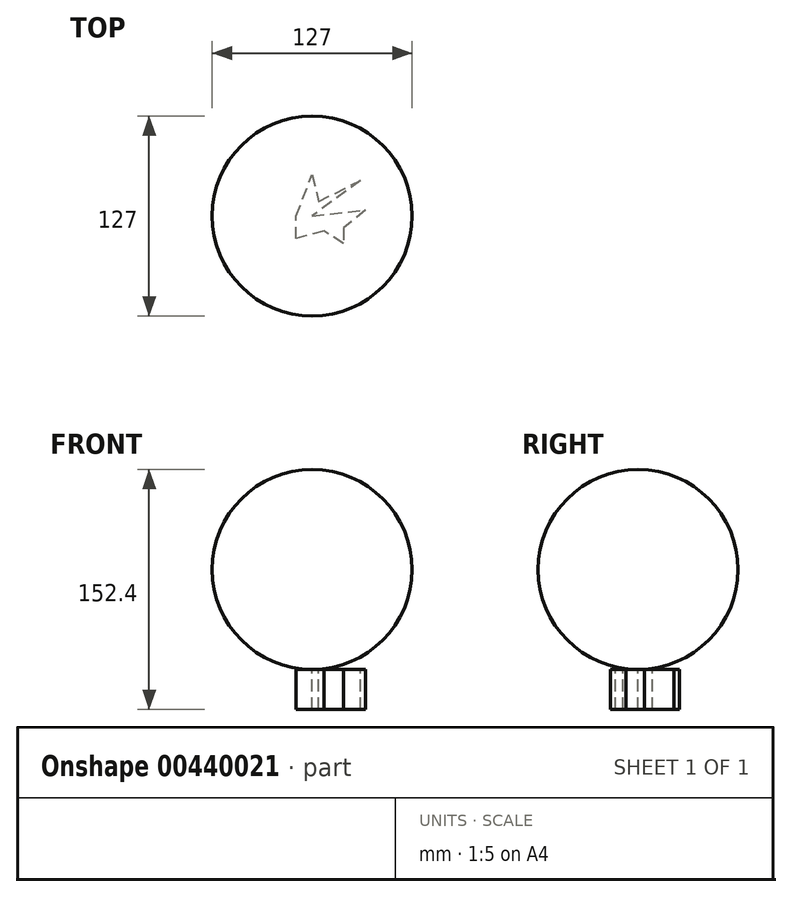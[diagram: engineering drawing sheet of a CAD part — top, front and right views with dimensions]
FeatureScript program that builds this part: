
annotation { "Feature Type Name" : "Feature", "Feature Type Description" : "" }
export const myFeature = defineFeature(function(context is Context, id is Id, definition is map)
    precondition{}
    {
        {
            var Q0;
            Q0=qCreatedBy(makeId("Top.planeOp"),FACE);
            var sketch = newSketch(context, id + "F0", { "sketchPlane" : qUnion([Q0])});
            skCircle(sketch, "E0", {"center": v(0, 0) * mm, "radius": 63.5 * mm});
            skSolve(sketch);
        }
        {
            var Q0;
            Q0=makeQuery(id+"F0.imprint","IMPRINT",FACE,{"disambiguationData":[TD([[makeQuery(id+"F0.imprint","IMPRINT",EDGE,{"derivedFrom":sQuery(id+"F0.wireOp",EDGE,"E0")}),1.0]])]});
            extrude(context, id + "F1", {"entities" : qUnion([Q0]), "depth" : 127 * mm});
        }
        {
            var Q0;
            Q0=makeQuery(id+"F1.opExtrude","CAP_EDGE",EDGE,{"disambiguationData":[OSD([sQuery(id+"F0.wireOp",EDGE,"E0")])],"isStart":false});
            var Q1;
            Q1=makeQuery(id+"F1.opExtrude","CAP_EDGE",EDGE,{"disambiguationData":[OSD([sQuery(id+"F0.wireOp",EDGE,"E0")])],"isStart":true});
            fillet(context, id + "F2", {"entities" : qUnion([Q0, Q1]), "radius" : 63.5 * mm, "tangentPropagation" : true, "allowEdgeOverflow" : false});
        }
        {
            var Q0;
            Q0=qCreatedBy(makeId("Top.planeOp"),FACE);
            var sketch = newSketch(context, id + "F3", { "sketchPlane" : qUnion([Q0])});
            skLineSegment(sketch, "E1", {"start": v(0, 0) * mm, "end": v(33.91, 3.95) * mm});
            skLineSegment(sketch, "E2", {"start": v(33.91, 3.95) * mm, "end": v(19.88, -7.66) * mm});
            skLineSegment(sketch, "E3", {"start": v(19.88, -7.66) * mm, "end": v(19.88, -17.6) * mm});
            skLineSegment(sketch, "E4", {"start": v(19.88, -17.6) * mm, "end": v(7.42, -9.46) * mm});
            skLineSegment(sketch, "E5", {"start": v(7.42, -9.46) * mm, "end": v(-10.1, -14.34) * mm});
            skLineSegment(sketch, "E6", {"start": v(-10.1, -14.34) * mm, "end": v(-10.1, 0) * mm});
            skLineSegment(sketch, "E7", {"start": v(-10.1, 0) * mm, "end": v(0, 26.25) * mm});
            skLineSegment(sketch, "E8", {"start": v(0, 26.25) * mm, "end": v(4.1, 9.25) * mm});
            skLineSegment(sketch, "E9", {"start": v(4.1, 9.25) * mm, "end": v(30.84, 22.68) * mm});
            skLineSegment(sketch, "E10", {"start": v(30.84, 22.68) * mm, "end": v(0, 0) * mm});
            skSolve(sketch);
        }
        {
            var Q0;
            Q0=makeQuery(id+"F3.imprint","IMPRINT",FACE,{"disambiguationData":[TD([[makeQuery(id+"F3.imprint","IMPRINT",EDGE,{"derivedFrom":sQuery(id+"F3.wireOp",EDGE,"E1")}),-1.0]])]});
            extrude(context, id + "F4", {"entities" : qUnion([Q0]), "operationType" : NewBodyOperationType.ADD, "oppositeDirection" : true, "depth" : 25.4 * mm});
        }
    });
